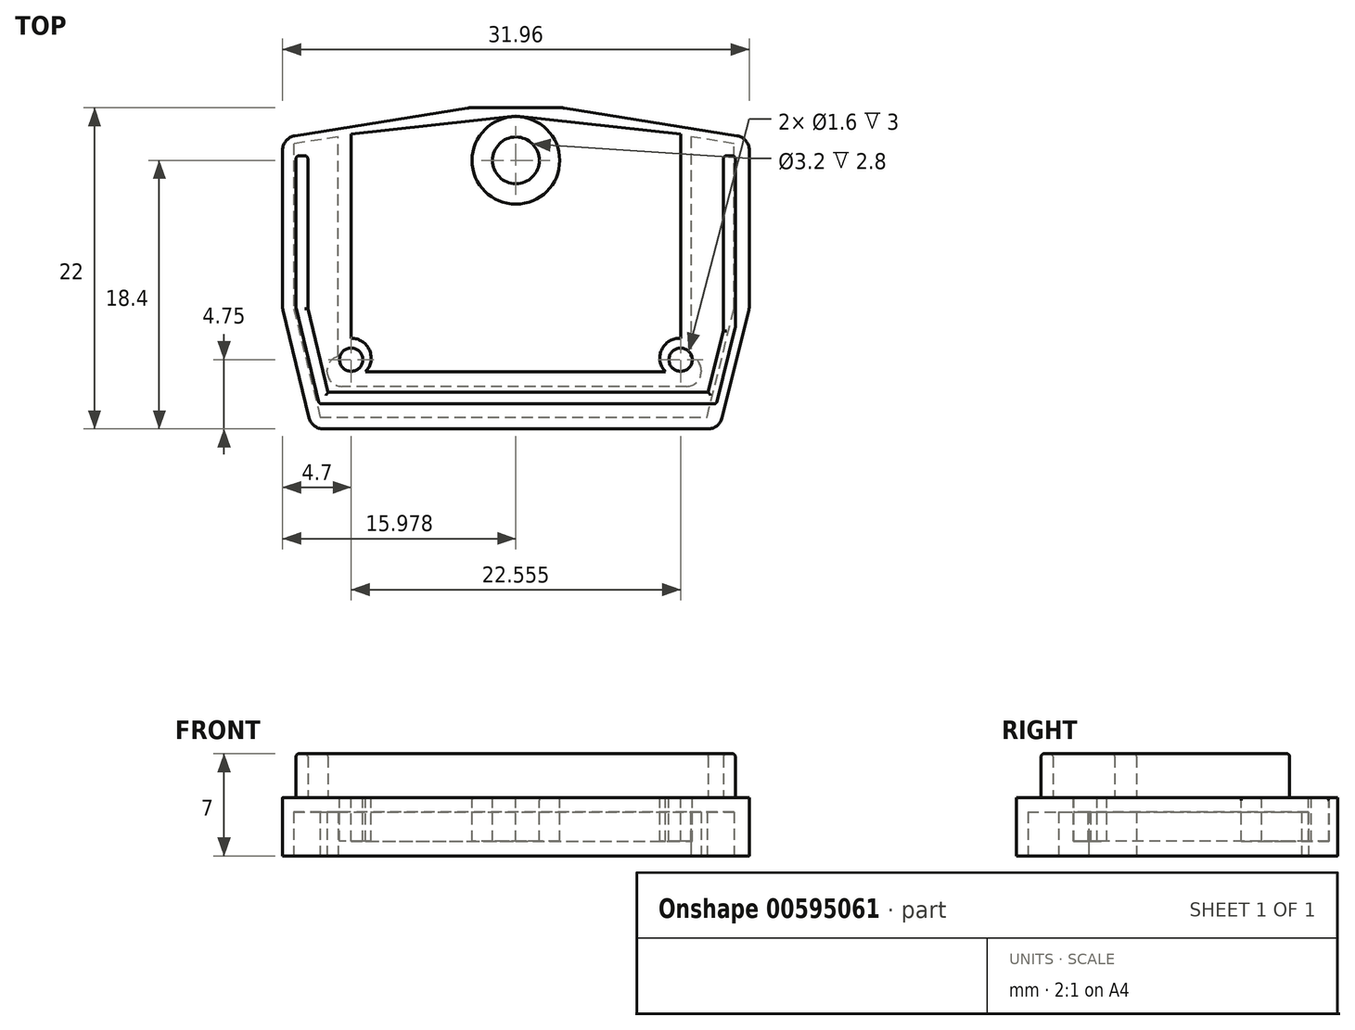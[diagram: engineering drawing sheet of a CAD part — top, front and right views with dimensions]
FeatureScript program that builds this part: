
annotation { "Feature Type Name" : "Feature", "Feature Type Description" : "" }
export const myFeature = defineFeature(function(context is Context, id is Id, definition is map)
    precondition{}
    {
        {
            var Q0;
            Q0=qCreatedBy(makeId("Top.planeOp"),FACE);
            var sketch = newSketch(context, id + "F0", { "sketchPlane" : qUnion([Q0])});
            skLineSegment(sketch, "E0", {"start": v(-28.61, 0) * mm, "end": v(-0.71, 0) * mm});
            skLineSegment(sketch, "E1", {"start": v(-0.71, 0) * mm, "end": v(1.34, 8.25) * mm});
            skLineSegment(sketch, "E2", {"start": v(-28.61, 0) * mm, "end": v(-30.62, 0) * mm});
            skLineSegment(sketch, "E3", {"start": v(-28.61, 0) * mm, "end": v(-30.62, 8.25) * mm});
            skLineSegment(sketch, "E4", {"start": v(-30.62, 8.25) * mm, "end": v(-30.62, 19.95) * mm});
            skLineSegment(sketch, "E5", {"start": v(1.34, 8.25) * mm, "end": v(1.34, 19.95) * mm});
            skLineSegment(sketch, "E6", {"start": v(-30.62, 19.95) * mm, "end": v(-17.88, 22) * mm});
            skLineSegment(sketch, "E7", {"start": v(1.34, 19.95) * mm, "end": v(-11.4, 22) * mm});
            skLineSegment(sketch, "E8", {"start": v(-17.88, 22) * mm, "end": v(-11.4, 22) * mm});
            skSolve(sketch);
        }
        {
            var Q0;
            Q0 = qSketchRegion(id + "F0", true);
            extrude(context, id + "F1", {"entities" : qUnion([Q0]), "depth" : 4 * mm, "offsetDistance" : 25 * mm});
        }
        {
            var Q0;
            Q0=makeQuery(id+"F1.opExtrude","CAP_FACE",FACE,{"disambiguationData":[OSD([sQuery(id+"F0.wireOp",EDGE,"E0"),sQuery(id+"F0.wireOp",EDGE,"E1"),sQuery(id+"F0.wireOp",EDGE,"E3"),sQuery(id+"F0.wireOp",EDGE,"E4"),sQuery(id+"F0.wireOp",EDGE,"E5"),sQuery(id+"F0.wireOp",EDGE,"E6"),sQuery(id+"F0.wireOp",EDGE,"E7"),sQuery(id+"F0.wireOp",EDGE,"E8")])],"isStart":false});
            var sketch = newSketch(context, id + "F2", { "sketchPlane" : qUnion([Q0])});
            skCircle(sketch, "E9", {"center": v(-14.64, 18.4) * mm, "radius": 1.6 * mm});
            skPoint(sketch, "E9.centerSnap0", {"position": v(-14.64, 22) * mm});
            skCircle(sketch, "E10", {"center": v(-25.92, 4.75) * mm, "radius": 0.8 * mm});
            skCircle(sketch, "E11", {"center": v(-3.36, 4.75) * mm, "radius": 0.8 * mm});
            skLineSegment(sketch, "E12", {"start": v(-25.92, 20.21) * mm, "end": v(-25.92, 6.21) * mm});
            skLineSegment(sketch, "E13", {"start": v(-3.36, 20.21) * mm, "end": v(-3.36, 6.21) * mm});
            skArc(sketch, "E14", {"start": v(-24.93, 3.92) * mm, "mid": v(-24.67, 5.4) * mm, "end": v(-25.92, 6.21) * mm});
            skArc(sketch, "E15", {"start": v(-3.36, 6.21) * mm, "mid": v(-4.67, 5.42) * mm, "end": v(-4.4, 3.92) * mm});
            skLineSegment(sketch, "E16", {"start": v(-24.93, 3.92) * mm, "end": v(-4.4, 3.92) * mm});
            skCircle(sketch, "E17", {"center": v(-14.64, 18.4) * mm, "radius": 3 * mm});
            skLineSegment(sketch, "E18", {"start": v(-25.92, 20.21) * mm, "end": v(-14.64, 21.45) * mm});
            skLineSegment(sketch, "E19", {"start": v(-14.64, 21.45) * mm, "end": v(-3.36, 20.21) * mm});
            skSolve(sketch);
        }
        {
            var Q0;
            Q0 = qSketchRegion(id + "F2", true);
            var Q1;
            Q1=makeQuery(id+"F2.imprint","IMPRINT",FACE,{"disambiguationData":[TD([[makeQuery(id+"F2.imprint","IMPRINT",EDGE,{"derivedFrom":sQuery(id+"F2.wireOp",EDGE,"E9")}),1.0]])]});
            extrude(context, id + "F3", {"entities" : qUnion([Q0, Q1]), "operationType" : NewBodyOperationType.REMOVE, "oppositeDirection" : true, "depth" : 3 * mm, "offsetDistance" : 25 * mm});
        }
        {
            var Q0;
            Q0=makeQuery(id+"F3.boolean.opBoolean","COPY",EDGE,{"derivedFrom":makeQuery(id+"F3.opExtrude","CAP_EDGE",EDGE,{"disambiguationData":[OSD([sQuery(id+"F2.wireOp",EDGE,"E17")])],"isStart":true})});
            var Q1;
            Q1=makeQuery(id+"F3.boolean.opBoolean","COPY",EDGE,{"derivedFrom":makeQuery(id+"F3.opExtrude","CAP_EDGE",EDGE,{"disambiguationData":[OSD([sQuery(id+"F2.wireOp",EDGE,"E9")])],"isStart":true})});
            var Q2;
            Q2=makeQuery(id+"F3.boolean.opBoolean","COPY",EDGE,{"derivedFrom":makeQuery(id+"F3.opExtrude","CAP_EDGE",EDGE,{"disambiguationData":[OSD([sQuery(id+"F2.wireOp",EDGE,"E11")])],"isStart":true})});
            var Q3;
            Q3=makeQuery(id+"F3.boolean.opBoolean","COPY",EDGE,{"derivedFrom":makeQuery(id+"F3.opExtrude","CAP_EDGE",EDGE,{"disambiguationData":[OSD([sQuery(id+"F2.wireOp",EDGE,"E10")])],"isStart":true})});
            fillet(context, id + "F4", {"entities" : qUnion([Q0, Q1, Q2, Q3]), "radius" : .2 * mm, "tangentPropagation" : true, "allowEdgeOverflow" : false});
        }
        {
            var Q0;
            {var subQ0=sQuery(id+"F0.wireOp",EDGE,"E8");var subQ1=sQuery(id+"F0.wireOp",EDGE,"E7");var subQ2=sQuery(id+"F0.wireOp",EDGE,"E6");var subQ3=sQuery(id+"F0.wireOp",EDGE,"E5");var subQ4=sQuery(id+"F0.wireOp",EDGE,"E0");var subQ5=sQuery(id+"F0.wireOp",EDGE,"E4");var subQ6=sQuery(id+"F0.wireOp",EDGE,"E1");var subQ7=sQuery(id+"F0.wireOp",EDGE,"E3");Q0=makeQuery(id+"F3.boolean.opBoolean","SPLIT",FACE,{"disambiguationData":[TD([makeQuery(id+"F1.opExtrude","SWEPT_FACE",FACE,{"disambiguationData":[OSD([subQ4])]})])],"derivedFrom":makeQuery(id+"F1.opExtrude","CAP_FACE",FACE,{"disambiguationData":[OSD([subQ4,subQ6,subQ7,subQ5,subQ3,subQ2,subQ1,subQ0])],"isStart":false})});}
            var sketch = newSketch(context, id + "F5", { "sketchPlane" : qUnion([Q0])});
            skLineSegment(sketch, "E20", {"start": v(-29.7, 18.71) * mm, "end": v(-29.7, 8.25) * mm});
            skLineSegment(sketch, "E21", {"start": v(-29.7, 8.25) * mm, "end": v(-28.1, 1.71) * mm});
            skLineSegment(sketch, "E22", {"start": v(0.38, 18.71) * mm, "end": v(0.38, 6.93) * mm});
            skLineSegment(sketch, "E23", {"start": v(0.38, 6.93) * mm, "end": v(-0.92, 1.71) * mm});
            skLineSegment(sketch, "E24", {"start": v(-28.1, 1.71) * mm, "end": v(-0.92, 1.71) * mm});
            skLineSegment(sketch, "E25", {"start": v(-29.7, 18.71) * mm, "end": v(-28.9, 18.71) * mm});
            skLineSegment(sketch, "E26", {"start": v(0.38, 18.71) * mm, "end": v(-0.42, 18.71) * mm});
            skLineSegment(sketch, "E27", {"start": v(-0.42, 18.71) * mm, "end": v(-0.42, 6.73) * mm});
            skLineSegment(sketch, "E28", {"start": v(-0.42, 6.73) * mm, "end": v(-1.47, 2.51) * mm});
            skLineSegment(sketch, "E29", {"start": v(-1.47, 2.51) * mm, "end": v(-15.1, 2.51) * mm});
            skLineSegment(sketch, "E30", {"start": v(-28.9, 18.71) * mm, "end": v(-28.9, 8.25) * mm});
            skLineSegment(sketch, "E31", {"start": v(-28.9, 8.25) * mm, "end": v(-27.5, 2.51) * mm});
            skLineSegment(sketch, "E32", {"start": v(-27.5, 2.51) * mm, "end": v(-15.1, 2.51) * mm});
            skSolve(sketch);
        }
        {
            var Q0;
            Q0 = qSketchRegion(id + "F5", true);
            extrude(context, id + "F6", {"entities" : qUnion([Q0]), "operationType" : NewBodyOperationType.ADD, "depth" : 3 * mm, "offsetDistance" : 25 * mm});
        }
        {
            var Q0;
            Q0=makeQuery(id+"F1.opExtrude","CAP_FACE",FACE,{"disambiguationData":[OSD([sQuery(id+"F0.wireOp",EDGE,"E0"),sQuery(id+"F0.wireOp",EDGE,"E1"),sQuery(id+"F0.wireOp",EDGE,"E3"),sQuery(id+"F0.wireOp",EDGE,"E4"),sQuery(id+"F0.wireOp",EDGE,"E5"),sQuery(id+"F0.wireOp",EDGE,"E6"),sQuery(id+"F0.wireOp",EDGE,"E7"),sQuery(id+"F0.wireOp",EDGE,"E8")])],"isStart":true});
            var sketch = newSketch(context, id + "F7", { "sketchPlane" : qUnion([Q0])});
            skLineSegment(sketch, "E33", {"start": v(-29.86, -19.54) * mm, "end": v(-29.86, -8.25) * mm});
            skLineSegment(sketch, "E34", {"start": v(-29.86, -8.25) * mm, "end": v(-28.05, -0.8) * mm});
            skLineSegment(sketch, "E35", {"start": v(-28.05, -0.8) * mm, "end": v(-1.56, -0.8) * mm});
            skLineSegment(sketch, "E36", {"start": v(-1.56, -0.8) * mm, "end": v(0.3, -8.25) * mm});
            skLineSegment(sketch, "E37", {"start": v(0.3, -8.25) * mm, "end": v(0.3, -19.54) * mm});
            skLineSegment(sketch, "E38", {"start": v(0.3, -19.54) * mm, "end": v(-2.67, -20.01) * mm});
            skLineSegment(sketch, "E39", {"start": v(-2.67, -20.01) * mm, "end": v(-2.67, -8.25) * mm});
            skLineSegment(sketch, "E40", {"start": v(-2.67, -8.25) * mm, "end": v(-2.67, -4.97) * mm});
            skLineSegment(sketch, "E41", {"start": v(-2.67, -4.97) * mm, "end": v(-1.95, -4.97) * mm});
            skLineSegment(sketch, "E42", {"start": v(-1.95, -4.97) * mm, "end": v(-1.95, -2.92) * mm});
            skLineSegment(sketch, "E43", {"start": v(-1.95, -2.92) * mm, "end": v(-27.57, -2.92) * mm});
            skLineSegment(sketch, "E44", {"start": v(-27.57, -2.92) * mm, "end": v(-27.57, -4.97) * mm});
            skPoint(sketch, "E44.endSnap0", {"position": v(-2.3, -4.97) * mm});
            skLineSegment(sketch, "E45", {"start": v(-27.57, -4.97) * mm, "end": v(-26.82, -4.97) * mm});
            skLineSegment(sketch, "E46", {"start": v(-26.82, -4.97) * mm, "end": v(-26.82, -20.01) * mm});
            skLineSegment(sketch, "E47", {"start": v(-26.82, -20.01) * mm, "end": v(-29.86, -19.54) * mm});
            skSolve(sketch);
        }
        {
            var Q0;
            Q0=makeQuery(id+"F7.imprint","IMPRINT",FACE,{"disambiguationData":[TD([[makeQuery(id+"F7.imprint","IMPRINT",EDGE,{"derivedFrom":sQuery(id+"F7.wireOp",EDGE,"E33")}),-1.0]])]});
            extrude(context, id + "F8", {"entities" : qUnion([Q0]), "operationType" : NewBodyOperationType.REMOVE, "oppositeDirection" : true, "depth" : 3 * mm, "offsetDistance" : 25 * mm});
        }
        {
            var Q0;
            Q0=makeQuery(id+"F8.boolean.opBoolean","COPY",EDGE,{"derivedFrom":makeQuery(id+"F8.opExtrude","SWEPT_EDGE",EDGE,{"disambiguationData":[OSD([sQuery(id+"F7.wireOp",EDGE,"E41"),sQuery(id+"F7.wireOp",EDGE,"E42")])]})});
            var Q1;
            Q1=makeQuery(id+"F8.boolean.opBoolean","COPY",EDGE,{"derivedFrom":makeQuery(id+"F8.opExtrude","SWEPT_EDGE",EDGE,{"disambiguationData":[OSD([sQuery(id+"F7.wireOp",EDGE,"E42"),sQuery(id+"F7.wireOp",EDGE,"E43")])]})});
            var Q2;
            Q2=makeQuery(id+"F8.boolean.opBoolean","COPY",EDGE,{"derivedFrom":makeQuery(id+"F8.opExtrude","SWEPT_EDGE",EDGE,{"disambiguationData":[OSD([sQuery(id+"F7.wireOp",EDGE,"E44"),sQuery(id+"F7.wireOp",EDGE,"E45")])]})});
            var Q3;
            Q3=makeQuery(id+"F8.boolean.opBoolean","COPY",EDGE,{"derivedFrom":makeQuery(id+"F8.opExtrude","SWEPT_EDGE",EDGE,{"disambiguationData":[OSD([sQuery(id+"F7.wireOp",EDGE,"E43"),sQuery(id+"F7.wireOp",EDGE,"E44")])]})});
            var Q4;
            Q4=makeQuery(id+"F1.opExtrude","SWEPT_EDGE",EDGE,{"disambiguationData":[OSD([sQuery(id+"F0.wireOp",EDGE,"E5"),sQuery(id+"F0.wireOp",EDGE,"E7")])]});
            var Q5;
            Q5=makeQuery(id+"F1.opExtrude","SWEPT_EDGE",EDGE,{"disambiguationData":[OSD([sQuery(id+"F0.wireOp",EDGE,"E1"),sQuery(id+"F0.wireOp",EDGE,"E5")])]});
            var Q6;
            Q6=makeQuery(id+"F1.opExtrude","SWEPT_EDGE",EDGE,{"disambiguationData":[OSD([sQuery(id+"F0.wireOp",EDGE,"E0"),sQuery(id+"F0.wireOp",EDGE,"E1")])]});
            var Q7;
            Q7=makeQuery(id+"F1.opExtrude","SWEPT_EDGE",EDGE,{"disambiguationData":[OSD([sQuery(id+"F0.wireOp",EDGE,"E0"),sQuery(id+"F0.wireOp",EDGE,"E3")])]});
            var Q8;
            Q8=makeQuery(id+"F1.opExtrude","SWEPT_EDGE",EDGE,{"disambiguationData":[OSD([sQuery(id+"F0.wireOp",EDGE,"E3"),sQuery(id+"F0.wireOp",EDGE,"E4")])]});
            var Q9;
            Q9=makeQuery(id+"F1.opExtrude","SWEPT_EDGE",EDGE,{"disambiguationData":[OSD([sQuery(id+"F0.wireOp",EDGE,"E4"),sQuery(id+"F0.wireOp",EDGE,"E6")])]});
            var Q10;
            Q10=makeQuery(id+"F1.opExtrude","SWEPT_EDGE",EDGE,{"disambiguationData":[OSD([sQuery(id+"F0.wireOp",EDGE,"E6"),sQuery(id+"F0.wireOp",EDGE,"E8")])]});
            var Q11;
            Q11=makeQuery(id+"F1.opExtrude","SWEPT_EDGE",EDGE,{"disambiguationData":[OSD([sQuery(id+"F0.wireOp",EDGE,"E7"),sQuery(id+"F0.wireOp",EDGE,"E8")])]});
            fillet(context, id + "F9", {"entities" : qUnion([Q0, Q1, Q2, Q3, Q4, Q5, Q6, Q7, Q8, Q9, Q10, Q11]), "radius" : 1 * mm, "tangentPropagation" : true, "allowEdgeOverflow" : false});
        }
        {
            var Q0;
            Q0=makeQuery(id+"F6.opExtrude","CAP_EDGE",EDGE,{"disambiguationData":[OSD([sQuery(id+"F5.wireOp",EDGE,"E20")])],"isStart":false});
            var Q1;
            Q1=makeQuery(id+"F6.opExtrude","CAP_EDGE",EDGE,{"disambiguationData":[OSD([sQuery(id+"F5.wireOp",EDGE,"E30")])],"isStart":false});
            var Q2;
            Q2=makeQuery(id+"F6.opExtrude","CAP_EDGE",EDGE,{"disambiguationData":[OSD([sQuery(id+"F5.wireOp",EDGE,"E25")])],"isStart":false});
            var Q3;
            Q3=makeQuery(id+"F6.opExtrude","CAP_EDGE",EDGE,{"disambiguationData":[OSD([sQuery(id+"F5.wireOp",EDGE,"E21")])],"isStart":false});
            var Q4;
            Q4=makeQuery(id+"F6.opExtrude","CAP_EDGE",EDGE,{"disambiguationData":[OSD([sQuery(id+"F5.wireOp",EDGE,"E31")])],"isStart":false});
            var Q5;
            Q5=makeQuery(id+"F6.opExtrude","CAP_FACE",FACE,{"disambiguationData":[OSD([sQuery(id+"F5.wireOp",EDGE,"E20"),sQuery(id+"F5.wireOp",EDGE,"E21"),sQuery(id+"F5.wireOp",EDGE,"E22"),sQuery(id+"F5.wireOp",EDGE,"E23"),sQuery(id+"F5.wireOp",EDGE,"E24"),sQuery(id+"F5.wireOp",EDGE,"E25"),sQuery(id+"F5.wireOp",EDGE,"E26"),sQuery(id+"F5.wireOp",EDGE,"E27"),sQuery(id+"F5.wireOp",EDGE,"E28"),sQuery(id+"F5.wireOp",EDGE,"E29"),sQuery(id+"F5.wireOp",EDGE,"E30"),sQuery(id+"F5.wireOp",EDGE,"E31"),sQuery(id+"F5.wireOp",EDGE,"E32")])],"isStart":false});
            var Q6;
            Q6=makeQuery(id+"F6.opExtrude","SWEPT_EDGE",EDGE,{"disambiguationData":[OSD([sQuery(id+"F5.wireOp",EDGE,"E21"),sQuery(id+"F5.wireOp",EDGE,"E24")])]});
            var Q7;
            Q7=makeQuery(id+"F6.opExtrude","SWEPT_EDGE",EDGE,{"disambiguationData":[OSD([sQuery(id+"F5.wireOp",EDGE,"E23"),sQuery(id+"F5.wireOp",EDGE,"E24")])]});
            var Q8;
            Q8=makeQuery(id+"F6.opExtrude","SWEPT_EDGE",EDGE,{"disambiguationData":[OSD([sQuery(id+"F5.wireOp",EDGE,"E22"),sQuery(id+"F5.wireOp",EDGE,"E23")])]});
            var Q9;
            Q9=makeQuery(id+"F6.opExtrude","SWEPT_EDGE",EDGE,{"disambiguationData":[OSD([sQuery(id+"F5.wireOp",EDGE,"E20"),sQuery(id+"F5.wireOp",EDGE,"E21")])]});
            var Q10;
            Q10=makeQuery(id+"F6.opExtrude","SWEPT_EDGE",EDGE,{"disambiguationData":[OSD([sQuery(id+"F5.wireOp",EDGE,"E20"),sQuery(id+"F5.wireOp",EDGE,"E25")])]});
            var Q11;
            Q11=makeQuery(id+"F6.opExtrude","SWEPT_EDGE",EDGE,{"disambiguationData":[OSD([sQuery(id+"F5.wireOp",EDGE,"E25"),sQuery(id+"F5.wireOp",EDGE,"E30")])]});
            var Q12;
            Q12=makeQuery(id+"F6.opExtrude","SWEPT_EDGE",EDGE,{"disambiguationData":[OSD([sQuery(id+"F5.wireOp",EDGE,"E22"),sQuery(id+"F5.wireOp",EDGE,"E26")])]});
            var Q13;
            Q13=makeQuery(id+"F6.opExtrude","SWEPT_EDGE",EDGE,{"disambiguationData":[OSD([sQuery(id+"F5.wireOp",EDGE,"E26"),sQuery(id+"F5.wireOp",EDGE,"E27")])]});
            fillet(context, id + "F10", {"entities" : qUnion([Q0, Q1, Q2, Q3, Q4, Q5, Q6, Q7, Q8, Q9, Q10, Q11, Q12, Q13]), "radius" : .2 * mm, "tangentPropagation" : true, "allowEdgeOverflow" : false});
        }
    });
